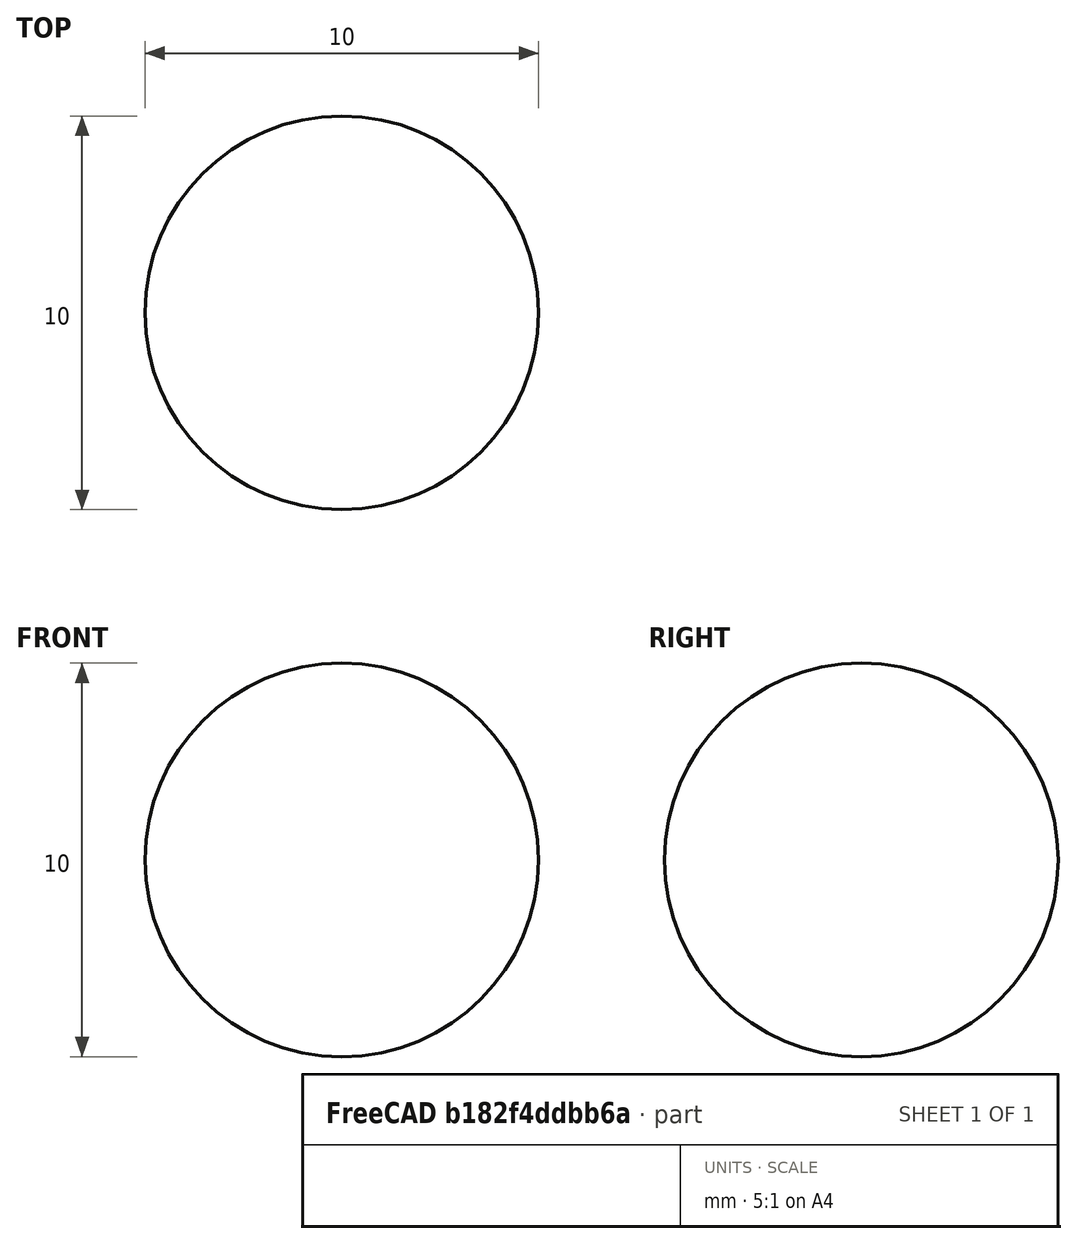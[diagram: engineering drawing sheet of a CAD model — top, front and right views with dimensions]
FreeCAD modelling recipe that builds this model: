
FCSTD DOCUMENT  (FreeCAD 0.19R24276 (Git))
Label: follow_path
License: All rights reserved
LicenseURL: http://en.wikipedia.org/wiki/All_rights_reserved
objects: Part::Part2DObjectPython×4, Part::Sphere×1
note: 5 computed .brp shape members not serialized (recipe doc carries the construction recipe); baked Part::Feature solids carry a one-line shape summary decoded from their .brp

FEATURE [Part::Part2DObjectPython] BezCurve  # Draft 2D object (typed FeaturePython)
  Area = 0
  Closed = false
  Degree = 4
  Length = 60.2097
  MakeFace = true
  Placement = pos=(0,1.08505,-1e-16) rot=(1,0,0;3.14159rad)
  Points = (5) [(-20,-1.22465e-15,0),(-20,20,0),(0,20,0),(20,20,0),(20,1.22465e-15,0)]
FEATURE [Part::Part2DObjectPython] BezCurve001  # Draft 2D object (typed FeaturePython)
  Area = 0
  Closed = false
  Degree = 4
  Length = 60.2097
  MakeFace = true
  Placement = pos=(20,0,20) rot=(0,-1,0;1.5708rad)
  Points = (5) [(-20,-1.22465e-15,0),(-20,20,0),(0,20,0),(20,20,0),(20,1.22465e-15,0)]
FEATURE [Part::Part2DObjectPython] BezCurve002  # Draft 2D object (typed FeaturePython)
  Area = 0
  Closed = false
  Degree = 4
  Length = 60.2097
  MakeFace = true
  Placement = pos=(-3.8147e-06,-1.5906e-12,40) rot=(0,0,1;3.14159rad)
  Points = (5) [(-20,-1.22465e-15,0),(-20,20,0),(0,20,0),(20,20,0),(20,1.22465e-15,0)]
FEATURE [Part::Part2DObjectPython] BezCurve003  # Draft 2D object (typed FeaturePython)
  Area = 0
  Closed = false
  Degree = 4
  Length = 60.2097
  MakeFace = true
  Placement = pos=(-20,0,20) rot=(0,1,0;1.5708rad)
  Points = (5) [(-20,-1.22465e-15,0),(-20,20,0),(0,20,0),(20,20,0),(20,1.22465e-15,0)]
FEATURE [Part::Sphere] Sphere
  Angle1 = -90
  Angle2 = 90
  Angle3 = 360
  AttacherType = Attacher::AttachEngine3D
  Placement = pos=(-20,1.20935,0.0284325) rot=(0,0,1;0rad)
  Radius = 5
